# Revit family: IS_Ceraplus_B8654_BIM_DE
name_source: partatom
category: Plumbing Fixtures
revit_build: Autodesk Revit MEP 2015 (Build: 20140606_1530(x64)
units: mm (PartAtom-declared; Revit-internal decimal feet)

## types (1)
- B8654AA - IS Badespezialarmatur UP CERAPLUS, Bausatz 2, Ros.d 157mm, Chrom
    Assembly Code = C1030215
    BIMobject category = Bath & Spas
    BOSUseNativeGeometries = 1
    Brand url = http://www.idealstandard.co.uk
    Description = B8654AA CERAPLUS build-in bath shower lever operated
    EAN code = https://4015413323321
    Edition number = 1
    FaucetFunction = mixed
    FaucetOperation = leverhandle
    FaucetType = pillar
    FlushRate = 0 m³
    FlushingRate = 0
    IFC Classification = Valve
    IfcExportAs = IfcValveType
    IfcExportType = BRASSWARE BATH
    Installation instructions = http://www.idealspec.co.uk
    Manufacturer name = Ideal Standard
    ManufacturerURL = www.idealstandard.com
    Material = Brass
    Material main = Brassware
    Model = B8654AA
    ModelNumber = B8654AA
    NBS Reference Code = 35-65-70-05
    NBS Reference Description = Bath Systems
    Name = CERAPLUS build-in bath shower lever operated
    NettWeight = 1,55 kg
    Nominal height = 192
    Nominal width = 158
    NominalDepth = 0 mm  [stored 0 ft]
    NominalHeight = 192 mm  [stored 0.629921 ft]
    NominalLength = 0 mm  [stored 0 ft]
    NominalWidth = 158 mm  [stored 0.518373 ft]
    OmniClass Code = 23.45.55.22
    OmniClass Description = Mixing Faucets
    Product Guid = da94847a-1b4f-44de-8485-b18f52b76daa
    Product SKU = B8654
    Product data url = https://bimobject.com
    Product family = Sanitary
    Product group = Bath taps
    Product name = Ceraplus Bath & Shower Mixer Built-In  Kit2 Easy-Box
    Product url = www.idealstandard.de/produkte
    ProductInformation = www.idealstandard.de/produkte
    QR code = http://bimobject.com
    Shape = Sculptured
    Space = Internal
    SpareParts = www.idealstandard.de/ersatzteile
    Technical description = www.idealstandard.de/produkte
    URL = www.idealstandard.com
    Uniclass 2.0 Code = SS-35-65-70-05
    Uniclass 2.0 Description = Bath Systems
    Uniclass 2015 Code = Pr_40_20_87_07
    Uniclass 2015 Name = Bath manual water supply sets
    ValveMechanism = ceramic disc
    ValveOperation = lever
    Version = 1
    VolumeUnits = Litres
    WarrantyDurationParts = 5
    WarrantyDurationUnit = year
    Weight Net (Kg) = 1.55
    WorkingPressure = 1-5 Bar

note: [stored X ft] marks values corroborated as IEEE doubles in the binary element streams (Revit-internal decimal feet)

## geometry (parser evidence)
native form markers: Blend x4, Sweep x1
no freeform markers — native parametric forms only
